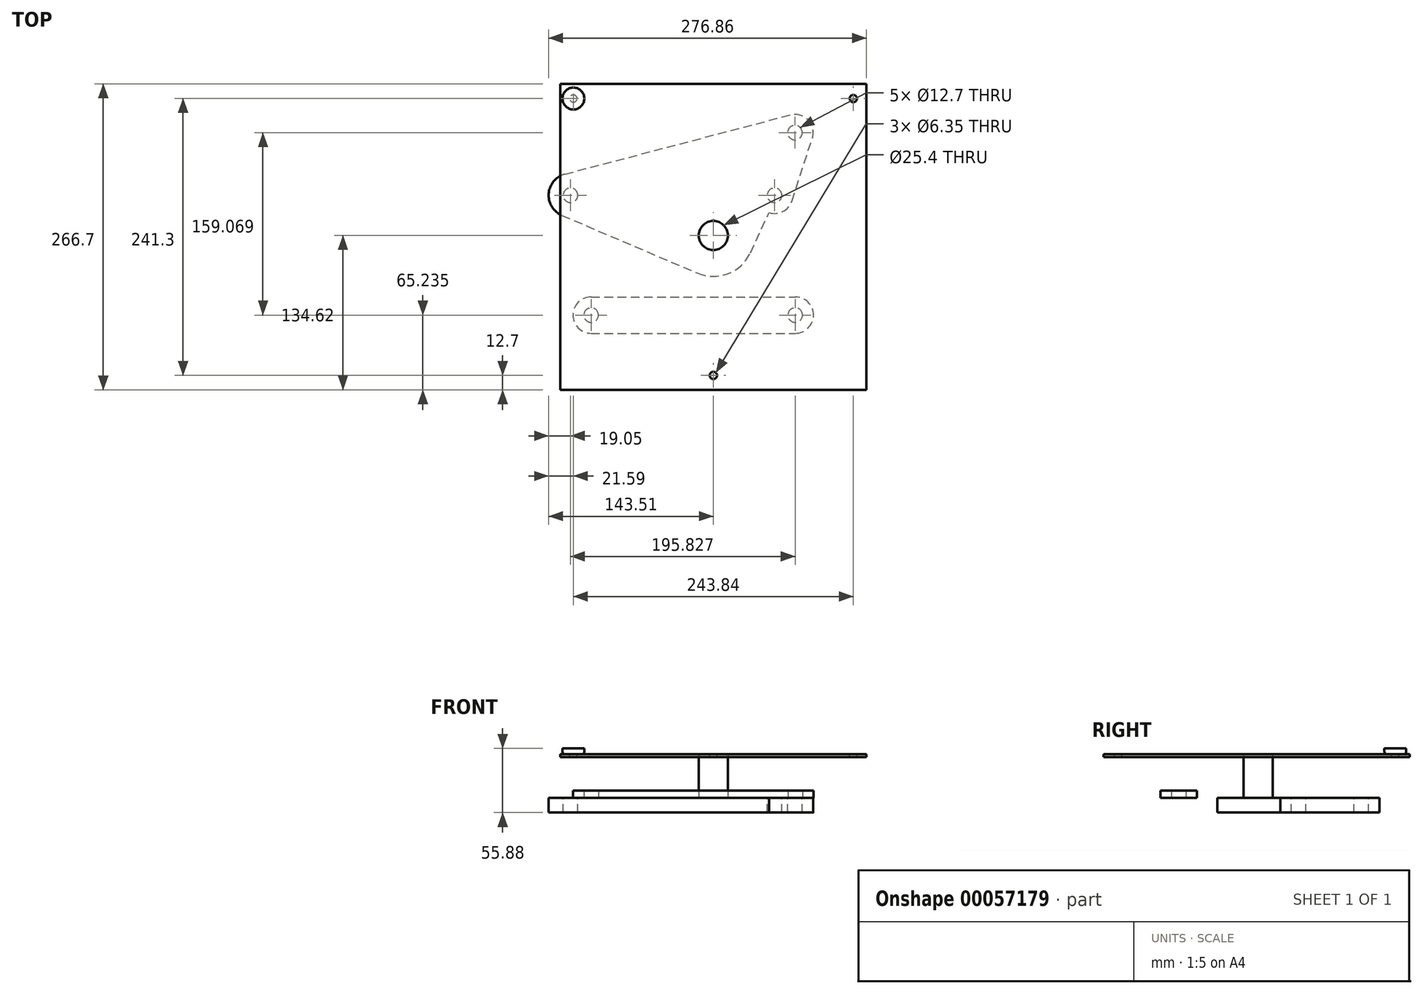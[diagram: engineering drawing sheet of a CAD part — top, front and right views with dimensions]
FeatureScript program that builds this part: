
annotation { "Feature Type Name" : "Feature", "Feature Type Description" : "" }
export const myFeature = defineFeature(function(context is Context, id is Id, definition is map)
    precondition{}
    {
        {
            var Q0;
            Q0=qCreatedBy(makeId("Top.planeOp"),FACE);
            var sketch = newSketch(context, id + "F0", { "sketchPlane" : qUnion([Q0])});
            skCircle(sketch, "E0", {"center": v(0, 0) * mm, "radius": 12.7 * mm});
            skPoint(sketch, "E1", {"position": v(71.12, 89.68) * mm});
            skPoint(sketch, "E2", {"position": v(53.34, 35.05) * mm});
            skPoint(sketch, "E3", {"position": v(-124.46, 35.05) * mm});
            skCircle(sketch, "E4", {"center": v(0, 0) * mm, "radius": 35.62 * mm});
            skCircle(sketch, "E5", {"center": v(53.34, 35.05) * mm, "radius": 15.88 * mm});
            skCircle(sketch, "E6", {"center": v(71.12, 89.68) * mm, "radius": 15.88 * mm});
            skCircle(sketch, "E7", {"center": v(-124.46, 35.05) * mm, "radius": 19.05 * mm});
            skCircle(sketch, "E8", {"center": v(-124.46, 35.05) * mm, "radius": 6.35 * mm});
            skCircle(sketch, "E9", {"center": v(53.34, 35.05) * mm, "radius": 6.35 * mm});
            skCircle(sketch, "E10", {"center": v(71.12, 89.68) * mm, "radius": 6.35 * mm});
            skLineSegment(sketch, "E11", {"start": v(-131.93, 17.52) * mm, "end": v(-13.97, -32.77) * mm});
            skLineSegment(sketch, "E12", {"start": v(32.29, -15.06) * mm, "end": v(48.59, 19.9) * mm});
            skLineSegment(sketch, "E13", {"start": v(68.44, 30.14) * mm, "end": v(86.22, 84.77) * mm});
            skLineSegment(sketch, "E14", {"start": v(-129.3, 53.47) * mm, "end": v(67.09, 105.04) * mm});
            skSolve(sketch);
        }
        {
            var Q0;
            {var subQ2=sQuery(id+"F0.wireOp",EDGE,"E11");Q0=makeQuery(id+"F0.imprint","IMPRINT",FACE,{"disambiguationData":[TD([[makeQuery(id+"F0.imprint","IMPRINT",EDGE,{"derivedFrom":subQ2}),1.0]])]});}
            var Q1;
            Q1=makeQuery(id+"F0.imprint","IMPRINT",FACE,{"disambiguationData":[TD([[makeQuery(id+"F0.imprint","IMPRINT",EDGE,{"derivedFrom":sQuery(id+"F0.wireOp",EDGE,"E8")}),-1.0]])]});
            var Q2;
            Q2=makeQuery(id+"F0.imprint","IMPRINT",FACE,{"disambiguationData":[TD([[makeQuery(id+"F0.imprint","IMPRINT",EDGE,{"derivedFrom":sQuery(id+"F0.wireOp",EDGE,"E0")}),-1.0]])]});
            var Q3;
            {var subQ4=sQuery(id+"F0.wireOp",EDGE,"E5");var subQ8=makeQuery(id+"F0.imprint","INTERSECT",VERTEX,{"derivedFrom":[subQ4,sQuery(id+"F0.wireOp",EDGE,"E12")]});Q3=makeQuery(id+"F0.imprint","IMPRINT",FACE,{"disambiguationData":[TD([[makeQuery(id+"F0.imprint","IMPRINT",EDGE,{"disambiguationData":[TD([[subQ8,1.0]])],"derivedFrom":subQ4}),1.0]])]});}
            var Q4;
            {var subQ0=sQuery(id+"F0.wireOp",EDGE,"E13");Q4=makeQuery(id+"F0.imprint","IMPRINT",FACE,{"disambiguationData":[TD([[makeQuery(id+"F0.imprint","IMPRINT",EDGE,{"derivedFrom":subQ0}),1.0]])]});}
            var Q5;
            {var subQ0=sQuery(id+"F0.wireOp",EDGE,"E10");var subQ1=sQuery(id+"F0.wireOp",EDGE,"E5");var subQ3=makeQuery(id+"F0.imprint","INTERSECT",VERTEX,{"disambiguationData":[OD(0.0)],"derivedFrom":[subQ1,subQ0]});Q5=makeQuery(id+"F0.imprint","IMPRINT",FACE,{"disambiguationData":[TD([[makeQuery(id+"F0.imprint","IMPRINT",EDGE,{"disambiguationData":[TD([[subQ3,1.0]])],"derivedFrom":subQ1}),-1.0]])]});}
            var Q6;
            {var subQ0=sQuery(id+"F0.wireOp",EDGE,"E10");var subQ1=sQuery(id+"F0.wireOp",EDGE,"E5");var subQ3=makeQuery(id+"F0.imprint","INTERSECT",VERTEX,{"disambiguationData":[OD(0.0)],"derivedFrom":[subQ1,subQ0]});Q6=makeQuery(id+"F0.imprint","IMPRINT",FACE,{"disambiguationData":[TD([[makeQuery(id+"F0.imprint","IMPRINT",EDGE,{"disambiguationData":[TD([[subQ3,1.0]])],"derivedFrom":subQ1}),1.0]])]});}
            var Q7;
            Q7=makeQuery(id+"F0.imprint","IMPRINT",FACE,{"disambiguationData":[TD([[makeQuery(id+"F0.imprint","IMPRINT",EDGE,{"derivedFrom":sQuery(id+"F0.wireOp",EDGE,"E0")}),1.0]])]});
            var Q8;
            Q8=makeQuery(id+"F0.imprint","IMPRINT",FACE,{"disambiguationData":[TD([[makeQuery(id+"F0.imprint","IMPRINT",EDGE,{"derivedFrom":sQuery(id+"F0.wireOp",EDGE,"E10")}),-1.0]])]});
            extrude(context, id + "F1", {"entities" : qUnion([Q0, Q1, Q2, Q3, Q4, Q5, Q6, Q7, Q8]), "oppositeDirection" : true, "depth" : 12.7 * mm});
        }
        {
            var Q0;
            Q0=makeQuery(id+"F0.imprint","IMPRINT",FACE,{"disambiguationData":[TD([[makeQuery(id+"F0.imprint","IMPRINT",EDGE,{"derivedFrom":sQuery(id+"F0.wireOp",EDGE,"E0")}),1.0]])]});
            extrude(context, id + "F2", {"entities" : qUnion([Q0]), "operationType" : NewBodyOperationType.ADD, "depth" : 38.1 * mm});
        }
        {
            var Q0;
            Q0=qCreatedBy(makeId("Top.planeOp"),FACE);
            var sketch = newSketch(context, id + "F3", { "sketchPlane" : qUnion([Q0])});
            skCircle(sketch, "E15", {"center": v(-106.43, -69.39) * mm, "radius": 15.88 * mm});
            skCircle(sketch, "E16", {"center": v(71.37, -69.39) * mm, "radius": 15.88 * mm});
            skLineSegment(sketch, "E17", {"start": v(-106.43, -53.51) * mm, "end": v(71.37, -53.51) * mm});
            skLineSegment(sketch, "E18", {"start": v(-106.43, -85.26) * mm, "end": v(71.37, -85.26) * mm});
            skCircle(sketch, "E19", {"center": v(-106.43, -69.39) * mm, "radius": 6.35 * mm});
            skCircle(sketch, "E20", {"center": v(71.37, -69.39) * mm, "radius": 6.35 * mm});
            skSolve(sketch);
        }
        {
            var Q0;
            Q0=makeQuery(id+"F3.imprint","IMPRINT",FACE,{"disambiguationData":[TD([[makeQuery(id+"F3.imprint","IMPRINT",EDGE,{"derivedFrom":sQuery(id+"F3.wireOp",EDGE,"E19")}),-1.0]])]});
            var Q1;
            {var subQ1=sQuery(id+"F3.wireOp",EDGE,"E17");Q1=makeQuery(id+"F3.imprint","IMPRINT",FACE,{"disambiguationData":[TD([[makeQuery(id+"F3.imprint","IMPRINT",EDGE,{"derivedFrom":subQ1}),-1.0]])]});}
            var Q2;
            Q2=makeQuery(id+"F3.imprint","IMPRINT",FACE,{"disambiguationData":[TD([[makeQuery(id+"F3.imprint","IMPRINT",EDGE,{"derivedFrom":sQuery(id+"F3.wireOp",EDGE,"E20")}),-1.0]])]});
            extrude(context, id + "F4", {"entities" : qUnion([Q0, Q1, Q2]), "depth" : 6.35 * mm});
        }
        {
            var Q0;
            Q0=makeQuery(id+"F2.opExtrude","CAP_FACE",FACE,{"disambiguationData":[OSD([sQuery(id+"F0.wireOp",EDGE,"E0")])],"isStart":false});
            var sketch = newSketch(context, id + "F5", { "sketchPlane" : qUnion([Q0])});
            skLineSegment(sketch, "E21.bottom", {"start": v(-133.35, 132.08) * mm, "end": v(133.35, 132.08) * mm});
            skLineSegment(sketch, "E21.top", {"start": v(-133.35, -134.62) * mm, "end": v(133.35, -134.62) * mm});
            skLineSegment(sketch, "E21.left", {"start": v(-133.35, 132.08) * mm, "end": v(-133.35, -134.62) * mm});
            skLineSegment(sketch, "E21.right", {"start": v(133.35, 132.08) * mm, "end": v(133.35, -134.62) * mm});
            skCircle(sketch, "E22", {"center": v(-121.92, 119.38) * mm, "radius": 3.18 * mm});
            skCircle(sketch, "E23", {"center": v(121.92, 119.38) * mm, "radius": 3.18 * mm});
            skCircle(sketch, "E24", {"center": v(0, -121.92) * mm, "radius": 3.17 * mm});
            skCircle(sketch, "E25", {"center": v(-121.92, 119.38) * mm, "radius": 9.53 * mm});
            skCircle(sketch, "E26", {"center": v(121.92, 119.38) * mm, "radius": 9.53 * mm});
            skCircle(sketch, "E27", {"center": v(0, -121.92) * mm, "radius": 9.53 * mm});
            skSolve(sketch);
        }
        {
            var Q0;
            Q0=makeQuery(id+"F5.imprint","IMPRINT",FACE,{"disambiguationData":[TD([[makeQuery(id+"F5.imprint","IMPRINT",EDGE,{"derivedFrom":sQuery(id+"F5.wireOp",EDGE,"E21.bottom")}),-1.0]])]});
            var Q1;
            Q1=makeQuery(id+"F5.imprint","IMPRINT",FACE,{"disambiguationData":[TD([[makeQuery(id+"F5.imprint","IMPRINT",EDGE,{"derivedFrom":sQuery(id+"F5.wireOp",EDGE,"E22")}),-1.0]])]});
            var Q2;
            Q2=makeQuery(id+"F5.imprint","IMPRINT",FACE,{"disambiguationData":[TD([[makeQuery(id+"F5.imprint","IMPRINT",EDGE,{"derivedFrom":sQuery(id+"F5.wireOp",EDGE,"E23")}),-1.0]])]});
            var Q3;
            Q3=makeQuery(id+"F5.imprint","IMPRINT",FACE,{"disambiguationData":[TD([[makeQuery(id+"F5.imprint","IMPRINT",EDGE,{"derivedFrom":sQuery(id+"F5.wireOp",EDGE,"E24")}),-1.0]])]});
            extrude(context, id + "F6", {"entities" : qUnion([Q0, Q1, Q2, Q3]), "oppositeDirection" : true, "depth" : 2.54 * mm});
        }
        {
            var Q0;
            Q0=makeQuery(id+"F5.imprint","IMPRINT",FACE,{"disambiguationData":[TD([[makeQuery(id+"F5.imprint","IMPRINT",EDGE,{"derivedFrom":sQuery(id+"F5.wireOp",EDGE,"E22")}),-1.0]])]});
            var Q1;
            Q1=makeQuery(id+"F5.imprint","IMPRINT",FACE,{"disambiguationData":[TD([[makeQuery(id+"F5.imprint","IMPRINT",EDGE,{"derivedFrom":sQuery(id+"F5.wireOp",EDGE,"E22")}),1.0]])]});
            extrude(context, id + "F7", {"entities" : qUnion([Q0, Q1]), "depth" : 5.08 * mm});
        }
        {
            var Q0;
            Q0=makeQuery(id+"F7.opExtrude","CAP_EDGE",EDGE,{"disambiguationData":[OSD([sQuery(id+"F5.wireOp",EDGE,"E25")])],"isStart":true});
            fillet(context, id + "F8", {"entities" : qUnion([Q0]), "radius" : 2.54 * mm, "tangentPropagation" : true, "allowEdgeOverflow" : false});
        }
    });
